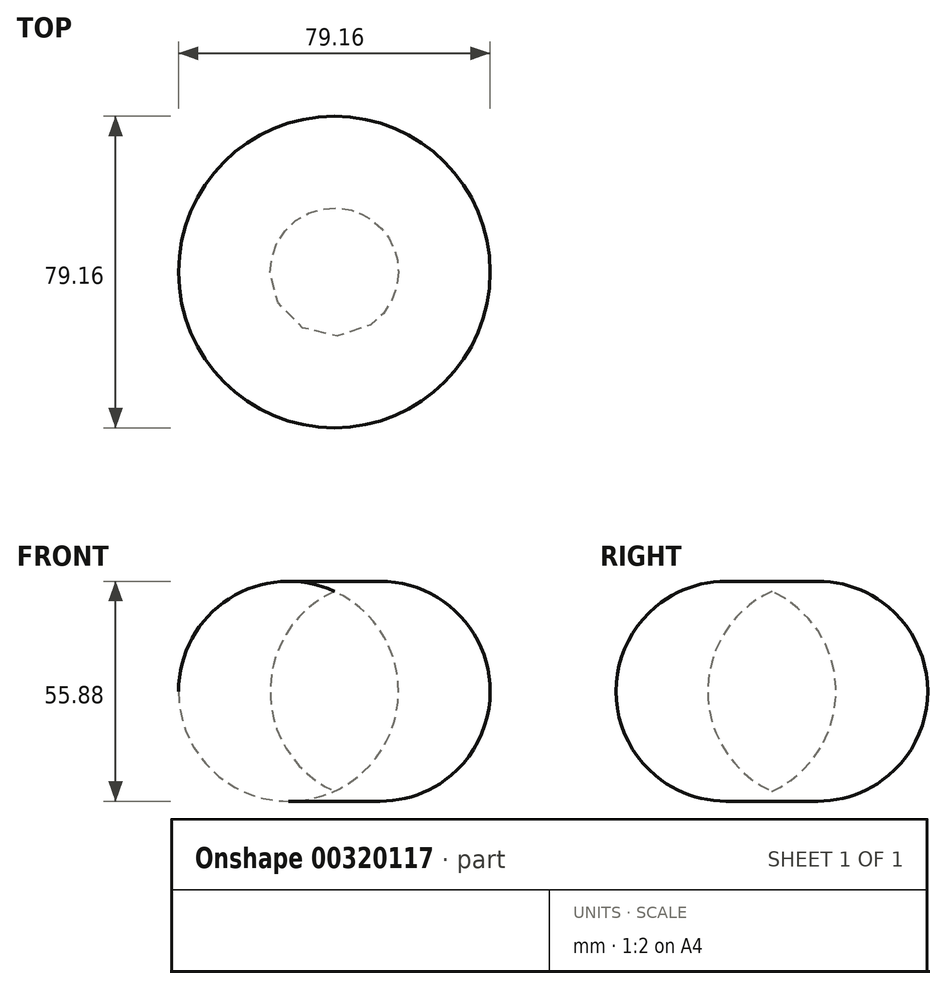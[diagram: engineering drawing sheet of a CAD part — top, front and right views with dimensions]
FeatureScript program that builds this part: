
annotation { "Feature Type Name" : "Feature", "Feature Type Description" : "" }
export const myFeature = defineFeature(function(context is Context, id is Id, definition is map)
    precondition{}
    {
        {
            var Q0;
            Q0=qCreatedBy(makeId("Front.planeOp"),FACE);
            var sketch = newSketch(context, id + "F0", { "sketchPlane" : qUnion([Q0])});
            skLineSegment(sketch, "E0", {"start": v(0, 0) * mm, "end": v(0, 50.8) * mm});
            skArc(sketch, "E1", {"start": v(0, 0) * mm, "mid": v(39.58, 25.4) * mm, "end": v(0, 50.8) * mm});
            skSolve(sketch);
        }
        {
            var Q0;
            Q0 = qSketchRegion(id + "F0", true);
            var Q1;
            Q1=sQuery(id+"F0.wireOp",EDGE,"E0");
            revolve(context, id + "F1", {"entities" : qUnion([Q0]), "axis" : qUnion([Q1]), "revolveType" : RevolveType.FULL});
        }
    });
